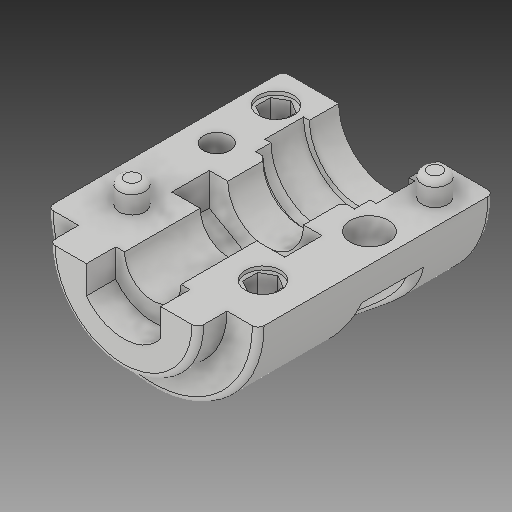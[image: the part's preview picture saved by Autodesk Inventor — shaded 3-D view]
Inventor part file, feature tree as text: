
AUTODESK INVENTOR PART (.ipt)
format: ipt  version: 2017 (Build 210142000, 142)  size: 266,240 bytes
history: native  units: in
note: dims shown in document units (in); Inventor stores cm internally (conversion verified against a paired STEP export)
features: fillet x1
ambient origin geometry x8: Origin, YZ Plane, XZ Plane, XY Plane, X Axis, Y Axis, Z Axis, Center Point
bodies: Solid1 (feature_tree)
feature tree (1):
  fillet  "Fillet1"  [1 undecoded]
note: 1 required parameter value undecoded (feature->parameter linkage not recoverable at this tier; creation-order binding heuristic only, values carry confidence <= 0.55)
